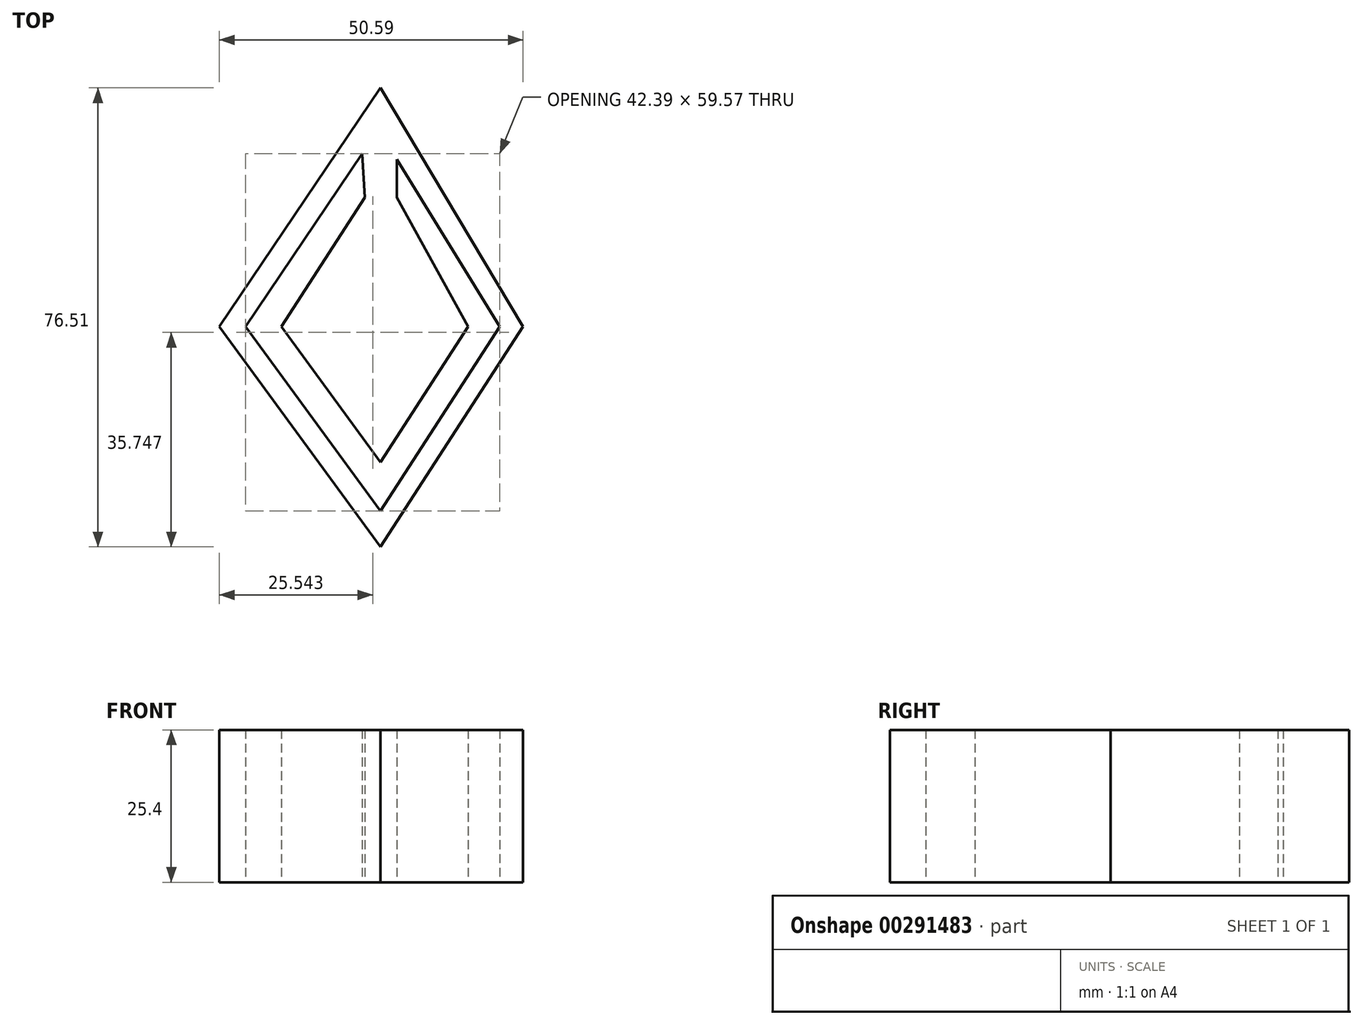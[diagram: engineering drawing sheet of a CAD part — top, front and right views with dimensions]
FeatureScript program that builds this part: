
annotation { "Feature Type Name" : "Feature", "Feature Type Description" : "" }
export const myFeature = defineFeature(function(context is Context, id is Id, definition is map)
    precondition{}
    {
        {
            var Q0;
            Q0=qCreatedBy(makeId("Top.planeOp"),FACE);
            var sketch = newSketch(context, id + "F0", { "sketchPlane" : qUnion([Q0])});
            skLineSegment(sketch, "E0", {"start": v(0, 39.78) * mm, "end": v(-26.82, 0) * mm});
            skLineSegment(sketch, "E1", {"start": v(-26.82, 0) * mm, "end": v(0, -36.73) * mm});
            skLineSegment(sketch, "E2", {"start": v(0, 39.78) * mm, "end": v(23.77, 0) * mm});
            skLineSegment(sketch, "E3", {"start": v(23.77, 0) * mm, "end": v(0, -36.73) * mm});
            skLineSegment(sketch, "E4", {"start": v(-3.05, 28.8) * mm, "end": v(-22.47, 0) * mm});
            skLineSegment(sketch, "E5", {"start": v(-22.47, 0) * mm, "end": v(0, -30.77) * mm});
            skLineSegment(sketch, "E6", {"start": v(0, -30.77) * mm, "end": v(19.92, 0) * mm});
            skLineSegment(sketch, "E7", {"start": v(19.92, 0) * mm, "end": v(2.74, 27.89) * mm});
            skLineSegment(sketch, "E8", {"start": v(2.74, 27.89) * mm, "end": v(2.74, 21.49) * mm});
            skLineSegment(sketch, "E9", {"start": v(2.74, 21.49) * mm, "end": v(14.63, 0) * mm});
            skLineSegment(sketch, "E10", {"start": v(14.63, 0) * mm, "end": v(0, -22.6) * mm});
            skLineSegment(sketch, "E11", {"start": v(0, -22.6) * mm, "end": v(-16.5, 0) * mm});
            skLineSegment(sketch, "E12", {"start": v(-16.5, 0) * mm, "end": v(-2.6, 21.49) * mm});
            skLineSegment(sketch, "E13", {"start": v(-2.6, 21.49) * mm, "end": v(-3.05, 28.8) * mm});
            skSolve(sketch);
        }
        {
            var Q0;
            Q0 = qSketchRegion(id + "F0", true);
            extrude(context, id + "F1", {"entities" : qUnion([Q0]), "depth" : 25.4 * mm});
        }
    });
